# Revit family: DBLTD_TheSenatorGroup_OfficeTables_Uku
name_source: partatom
category: Furniture
units: mm (PartAtom-declared; Revit-internal decimal feet)

## family parameters
Always vertical = Yes
Cut with Voids When Loaded = No
OmniClass Number = 23.40.20.00
OmniClass Title = General Furniture and Specialties
Render Appearance Source = Family Geometry
Room Calculation Point = No
Shared = Yes
Work Plane-Based = No

## types (1)
- Host Table
    Assembly Code = E2020200
    AssetType = Movable
    Category = Pr_40_50_21_60 Office tables
    Color = Wood Finishes: Solid Oak with Cleat Finish or Black (Stained). Metal Finishes: Black (Textured) or Dark Bronze (Textured).
    Constituents = Frame and Tabletop
    Cost = 0 $
    Default Elevation = 0 mm  [stored 0 ft]
    Description = Host Table
    DurationUnit = years
    ExpectedLife = 5
    Finish = Wood Finishes: Solid Oak with Cleat Finish or Black (Stained). Metal Finishes: Black (Textured) or Dark Bronze (Textured).
    Keynote = Pr_40_50_21_60 Office tables
    Manufacturer = The Senator Group
    ManufacturerName = The Senator Group
    ManufacturerURL = https://www.thesenatorgroup.com
    Material = Wood Finishes: Solid Oak with Cleat Finish or Black (Stained). Metal Finishes: Black (Textured) or Dark Bronze (Textured).
    Model = UKUHST
    ModelNumber = UKUHST
    ModelReference = Host Table
    Name = Table
    NominalDepth = 350 mm  [stored 1.14829 ft]
    NominalHeight = 640 mm  [stored 2.09974 ft]
    NominalWidth = 350 mm  [stored 1.14829 ft]
    NumberOfChairs = 0
    ProductInformation = https://www.allermuir.com
    Shape = Rectangular
    Size = 640 x 350 x 350 mm
    Type Comments = Host Table
    URL = https://www.thesenatorgroup.com
    Uniclass2015Code = Pr_40_50_21_60
    Uniclass2015Title = Office tables
    Uniclass2015Version = Products v1.15
    Version = 1
    WarrantyDescription = The Senator Group warrants that its manufactured products are free from manufacturing defects - in materials or workmanship - for a period of five (5) years.
    WarrantyDurationLabor = 5
    WarrantyDurationParts = 5
    WarrantyDurationUnit = years
    WarrantyGuarantorLabor = https://www.thesenatorgroup.com
    WarrantyGuarantorParts = https://www.thesenatorgroup.com
    WorksurfaceArea = 0 m²

note: [stored X ft] marks values corroborated as IEEE doubles in the binary element streams (Revit-internal decimal feet)

## geometry (parser evidence)
native form markers: Sweep x3
no freeform markers — native parametric forms only
